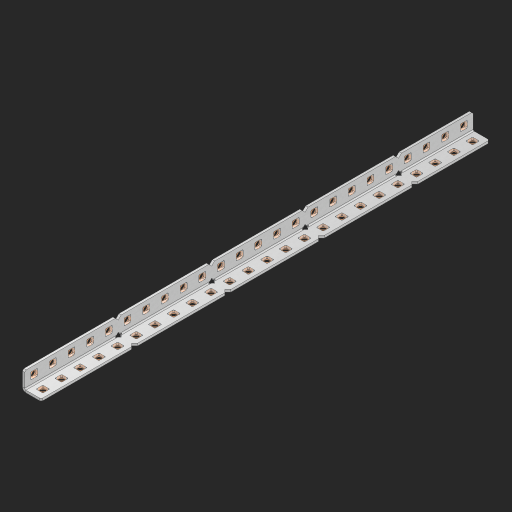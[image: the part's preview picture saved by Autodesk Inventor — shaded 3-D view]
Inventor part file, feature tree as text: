
AUTODESK INVENTOR PART (.ipt)
format: ipt  version: 2023 (Build 270158000, 158)  size: 886,784 bytes
history: native  units: in
note: dims shown in document units (in); Inventor stores cm internally (conversion verified against a paired STEP export)
features: other x54, extrude x49, sheet_metal_op x8, sketch x5, pattern_linear x1, mirror x1, chamfer x1
ambient origin geometry x8: Origin, YZ Plane, XZ Plane, XY Plane, X Axis, Y Axis, Z Axis, Center Point
bodies: Solid1 (feature_tree), Body (feature_tree)
feature tree (119):
  sheet_metal_op  "Flanges"
  sheet_metal_op  "Body Pattern"
  other  "Arc Length"
  pattern_linear  "Notch Pattern"  Spacing1=0.125in  [1 undecoded]
  other  "Diagonal Plane"
  mirror  "Everything Mirrored"
  chamfer  "End Chamfer"
  sketch  "Sketch1"  dims[d0=0.5in]
  other  "Plate1"
  sketch  "Sketch2"  dims[d1=12.0in]
  other  "Plate2"
  sheet_metal_op  "Bend1"
  sheet_metal_op  "Corner1"
  sketch  "Sketch8"  dims[d2=0.0625in]
  sketch  "Sketch9"  dims[d3=0.0625in]
  other  "Srf91"
  sheet_metal_op  "Body Pattern Sketch"
  other  "Srf92"
  sketch  "Sketch13"  dims[d4=0.0312in d5=0.125in d6=0.0625in d7=0.5in d8=90.0deg d9=0.0312in d10=0.25in d11=0.0625in d12=0.0625in d49=0.182in d50=0.02in d52=0.25in d53=0.0625in d54=0.0in d55=0.172in d56=1.0in d57=0.0in d85=0.1473in d86=0.1782in d89=0.0625in d90=0.0in d91=0.04in d92=0.0491in d95=2.5in d96=0.04in d97=0.25in d98=45.0deg d123=0.204in d126=0.0491in d127=0.1473in d128=0.08in d129=0.04in d130=2.5in d131=9.4488in d133=0.5in d134=0.3937in d136=1.0in]
  other  "Srf856"
  other  "Srf857"
  other  "Srf858"
  other  "Srf859"
  other  "Srf860"
  other  "Srf861"
  other  "Srf1275"
  other  "Srf1276"
  other  "Srf1278"
  other  "Srf1279"
  other  "Srf1280"
  other  "Srf1281"
  other  "Srf1282"
  other  "Srf1283"
  other  "Srf1383"
  other  "Srf1384"
  other  "Srf1385"
  other  "Srf1386"
  other  "Srf1387"
  other  "Srf1388"
  other  "Srf1389"
  other  "Srf1390"
  other  "Srf1391"
  other  "Srf1392"
  other  "Srf1393"
  other  "Srf1394"
  other  "Srf1395"
  other  "Srf1396"
  other  "Srf1397"
  other  "Srf1398"
  other  "Srf1399"
  other  "Srf1475"
  other  "Srf1476"
  other  "Srf1477"
  other  "Srf1478"
  other  "Srf1479"
  other  "Srf1480"
  other  "Srf1481"
  other  "Srf1482"
  other  "Srf1483"
  other  "Srf1484"
  other  "Srf1485"
  other  "Srf1486"
  other  "Srf1487"
  other  "Srf1488"
  other  "Srf1489"
  other  "Srf1490"
  other  "Srf1491"
  sheet_metal_op  "Body Stamp"
  sheet_metal_op  "Body Circle"
  sheet_metal_op  "Notch"
  extrude  "ExtrusionSrf92"  Depth=0.0625in
  extrude  "ExtrusionSrf856"  Depth=0.5in TaperAngle=90.0deg
  extrude  "ExtrusionSrf857"  Depth=0.25in
  extrude  "ExtrusionSrf858"  Depth=0.0625in
  extrude  "ExtrusionSrf859"  Depth=0.0625in
  extrude  "ExtrusionSrf860"  Depth=0.3937in
  extrude  "ExtrusionSrf861"  Depth=0.02in
  extrude  "ExtrusionSrf1275"  Depth=0.25in
  extrude  "ExtrusionSrf1276"  Depth=0.0625in
  extrude  "ExtrusionSrf1277"  TaperAngle=0.0deg  [1 undecoded]
  extrude  "ExtrusionSrf1278"  Depth=0.3937in
  extrude  "ExtrusionSrf1279"  Depth=0.3937in TaperAngle=0.0deg
  extrude  "ExtrusionSrf1280"  Depth=0.3937in
  extrude  "ExtrusionSrf1281"  Depth=0.3937in
  extrude  "ExtrusionSrf1282"  Depth=0.0625in
  extrude  "ExtrusionSrf1383"  Depth=0.3937in TaperAngle=0.0deg
  extrude  "ExtrusionSrf1384"  Depth=0.3937in
  extrude  "ExtrusionSrf1385"  Depth=0.25in TaperAngle=45.0deg
  extrude  "ExtrusionSrf1386"  Depth=0.3937in
  extrude  "ExtrusionSrf1387"  Depth=0.3937in
  extrude  "ExtrusionSrf1388"  Depth=0.3937in
  extrude  "ExtrusionSrf1389"  Depth=0.3937in
  extrude  "ExtrusionSrf1390"  Depth=0.3937in
  extrude  "ExtrusionSrf1391"  Depth=0.3937in
  extrude  "ExtrusionSrf1392"  Depth=0.3937in
  extrude  "ExtrusionSrf1393"  Depth=0.5in
  extrude  "ExtrusionSrf1394"  [1 undecoded]
  extrude  "ExtrusionSrf1395"  [1 undecoded]
  extrude  "ExtrusionSrf1396"  [1 undecoded]
  extrude  "ExtrusionSrf1397"  [1 undecoded]
  extrude  "ExtrusionSrf1398"  [1 undecoded]
  extrude  "ExtrusionSrf1399"  [1 undecoded]
  extrude  "ExtrusionSrf1475"  [1 undecoded]
  extrude  "ExtrusionSrf1476"  [1 undecoded]
  extrude  "ExtrusionSrf1477"  [1 undecoded]
  extrude  "ExtrusionSrf1478"  [1 undecoded]
  extrude  "ExtrusionSrf1479"  [1 undecoded]
  extrude  "ExtrusionSrf1480"  [1 undecoded]
  extrude  "ExtrusionSrf1481"  [1 undecoded]
  extrude  "ExtrusionSrf1482"  [1 undecoded]
  extrude  "ExtrusionSrf1483"  [1 undecoded]
  extrude  "ExtrusionSrf1484"  [1 undecoded]
  extrude  "ExtrusionSrf1485"  [1 undecoded]
  extrude  "ExtrusionSrf1486"  [1 undecoded]
  extrude  "ExtrusionSrf1487"  [1 undecoded]
  extrude  "ExtrusionSrf1488"  [1 undecoded]
  extrude  "ExtrusionSrf1489"  [1 undecoded]
  extrude  "ExtrusionSrf1490"  [1 undecoded]
  extrude  "ExtrusionSrf1491"  [1 undecoded]
note: 25 required parameter values undecoded (feature->parameter linkage not recoverable at this tier; creation-order binding heuristic only, values carry confidence <= 0.55)
